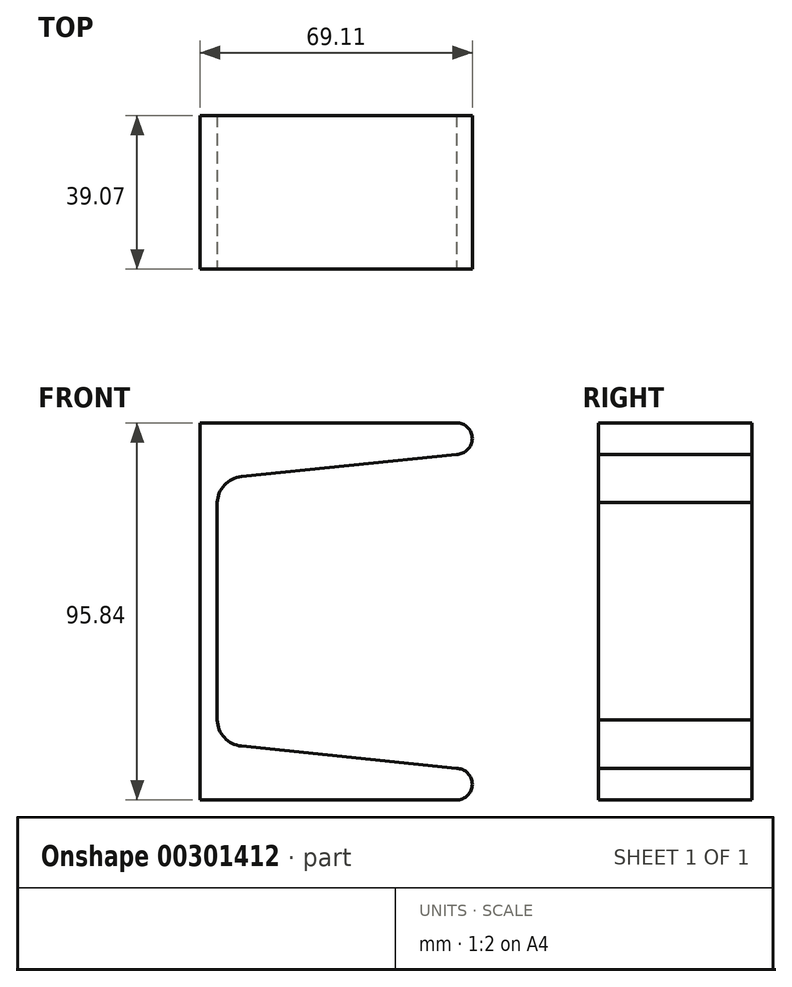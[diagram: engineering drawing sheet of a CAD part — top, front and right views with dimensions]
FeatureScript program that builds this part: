
annotation { "Feature Type Name" : "Feature", "Feature Type Description" : "" }
export const myFeature = defineFeature(function(context is Context, id is Id, definition is map)
    precondition{}
    {
        {
            var Q0;
            Q0=qCreatedBy(makeId("Front.planeOp"),FACE);
            var sketch = newSketch(context, id + "F0", { "sketchPlane" : qUnion([Q0])});
            skLineSegment(sketch, "E0", {"start": v(0, 0) * mm, "end": v(0, 47.92) * mm});
            skLineSegment(sketch, "E1", {"start": v(0, 47.92) * mm, "end": v(65.1, 47.92) * mm});
            skArc(sketch, "E2", {"start": v(65.1, 39.9) * mm, "mid": v(69.11, 43.9) * mm, "end": v(65.1, 47.92) * mm});
            skLineSegment(sketch, "E3", {"start": v(65.1, 39.9) * mm, "end": v(10.46, 34.23) * mm});
            skArc(sketch, "E4", {"start": v(10.46, 34.23) * mm, "mid": v(6.14, 32.08) * mm, "end": v(4.32, 27.62) * mm});
            skLineSegment(sketch, "E5", {"start": v(4.32, 27.62) * mm, "end": v(4.32, 0) * mm});
            skLineSegment(sketch, "E6.MirrorCS", {"start": v(0, 0) * mm, "end": v(0, -47.92) * mm});
            skArc(sketch, "E7.MirrorCS", {"start": v(10.46, -34.23) * mm, "mid": v(6.14, -32.08) * mm, "end": v(4.32, -27.62) * mm});
            skLineSegment(sketch, "E8.MirrorCS", {"start": v(4.32, -27.62) * mm, "end": v(4.32, 0) * mm});
            skLineSegment(sketch, "E9.MirrorCS", {"start": v(65.1, -39.9) * mm, "end": v(10.46, -34.23) * mm});
            skArc(sketch, "E10.MirrorCS", {"start": v(65.1, -39.9) * mm, "mid": v(69.11, -43.9) * mm, "end": v(65.1, -47.92) * mm});
            skLineSegment(sketch, "E11.MirrorCS", {"start": v(0, -47.92) * mm, "end": v(65.1, -47.92) * mm});
            skSolve(sketch);
        }
        {
            var Q0;
            Q0=qCreatedBy(makeId("Right.planeOp"),FACE);
            var sketch = newSketch(context, id + "F1", { "sketchPlane" : qUnion([Q0])});
            skLineSegment(sketch, "E12", {"start": v(0, 47.45) * mm, "end": v(-40.96, 47.45) * mm});
            skLineSegment(sketch, "E13", {"start": v(0, -49.34) * mm, "end": v(-39.07, -49.34) * mm});
            skSolve(sketch);
        }
        {
            var Q0;
            Q0=makeQuery(id+"F0.imprint","IMPRINT",FACE,{"disambiguationData":[TD([[makeQuery(id+"F0.imprint","IMPRINT",EDGE,{"derivedFrom":sQuery(id+"F0.wireOp",EDGE,"E0")}),-1.0]])]});
            var Q1;
            Q1=sQuery(id+"F1.wireOp",EDGE,"E13");
            sweep(context, id + "F2", {"profiles" : qUnion([Q0]), "path" : qUnion([Q1])});
        }
    });
